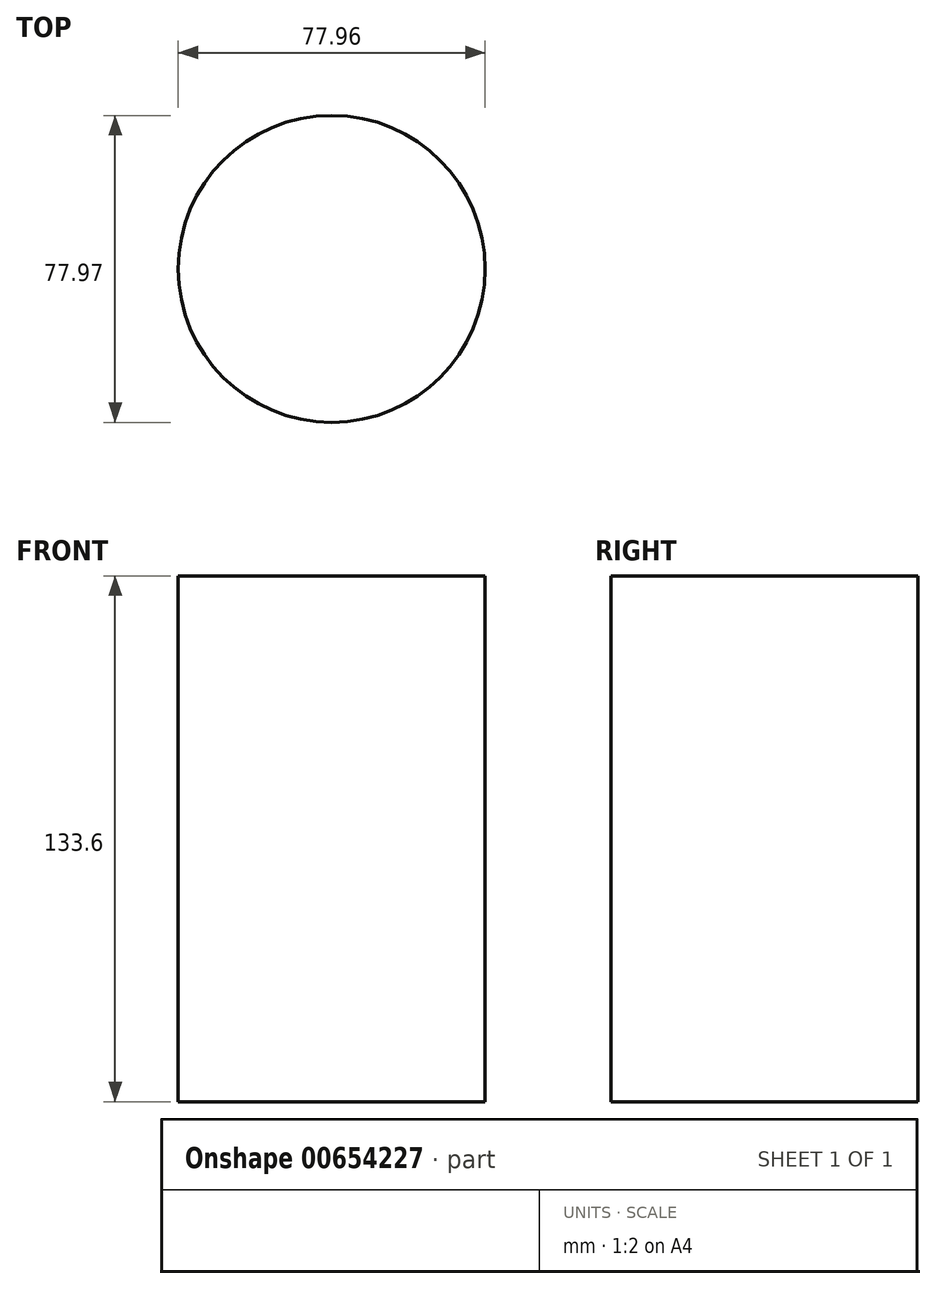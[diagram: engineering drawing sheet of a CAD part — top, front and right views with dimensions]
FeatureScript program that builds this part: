
annotation { "Feature Type Name" : "Feature", "Feature Type Description" : "" }
export const myFeature = defineFeature(function(context is Context, id is Id, definition is map)
    precondition{}
    {
        {
            var Q0;
            Q0=qCreatedBy(makeId("Top.planeOp"),FACE);
            var sketch = newSketch(context, id + "F0", { "sketchPlane" : qUnion([Q0])});
            skCircle(sketch, "E0", {"center": v(-36.3, 14.2) * mm, "radius": 38.98 * mm});
            skPoint(sketch, "E0.first.point", {"position": v(0, 0) * mm});
            skPoint(sketch, "E0.second.point", {"position": v(-67.98, 36.93) * mm});
            skPoint(sketch, "E0.third.point", {"position": v(-57.33, 47.03) * mm});
            skSolve(sketch);
        }
        {
            var Q0;
            Q0 = qSketchRegion(id + "F0", true);
            extrude(context, id + "F1", {"entities" : qUnion([Q0]), "depth" : 98.55 * mm, "offsetDistance" : 25.4 * mm});
        }
        {
            var Q0;
            Q0=makeQuery(id+"F1.opExtrude","CAP_FACE",FACE,{"disambiguationData":[OSD([sQuery(id+"F0.wireOp",EDGE,"E0")])],"isStart":true});
            var Q1;
            Q1=makeQuery(id+"F1.opExtrude","CAP_FACE",FACE,{"disambiguationData":[OSD([sQuery(id+"F0.wireOp",EDGE,"E0")])],"isStart":false});
            extrude(context, id + "F2", {"entities" : qUnion([Q0, Q1]), "operationType" : NewBodyOperationType.ADD, "depth" : 35.05 * mm, "offsetDistance" : 25.4 * mm});
        }
    });
